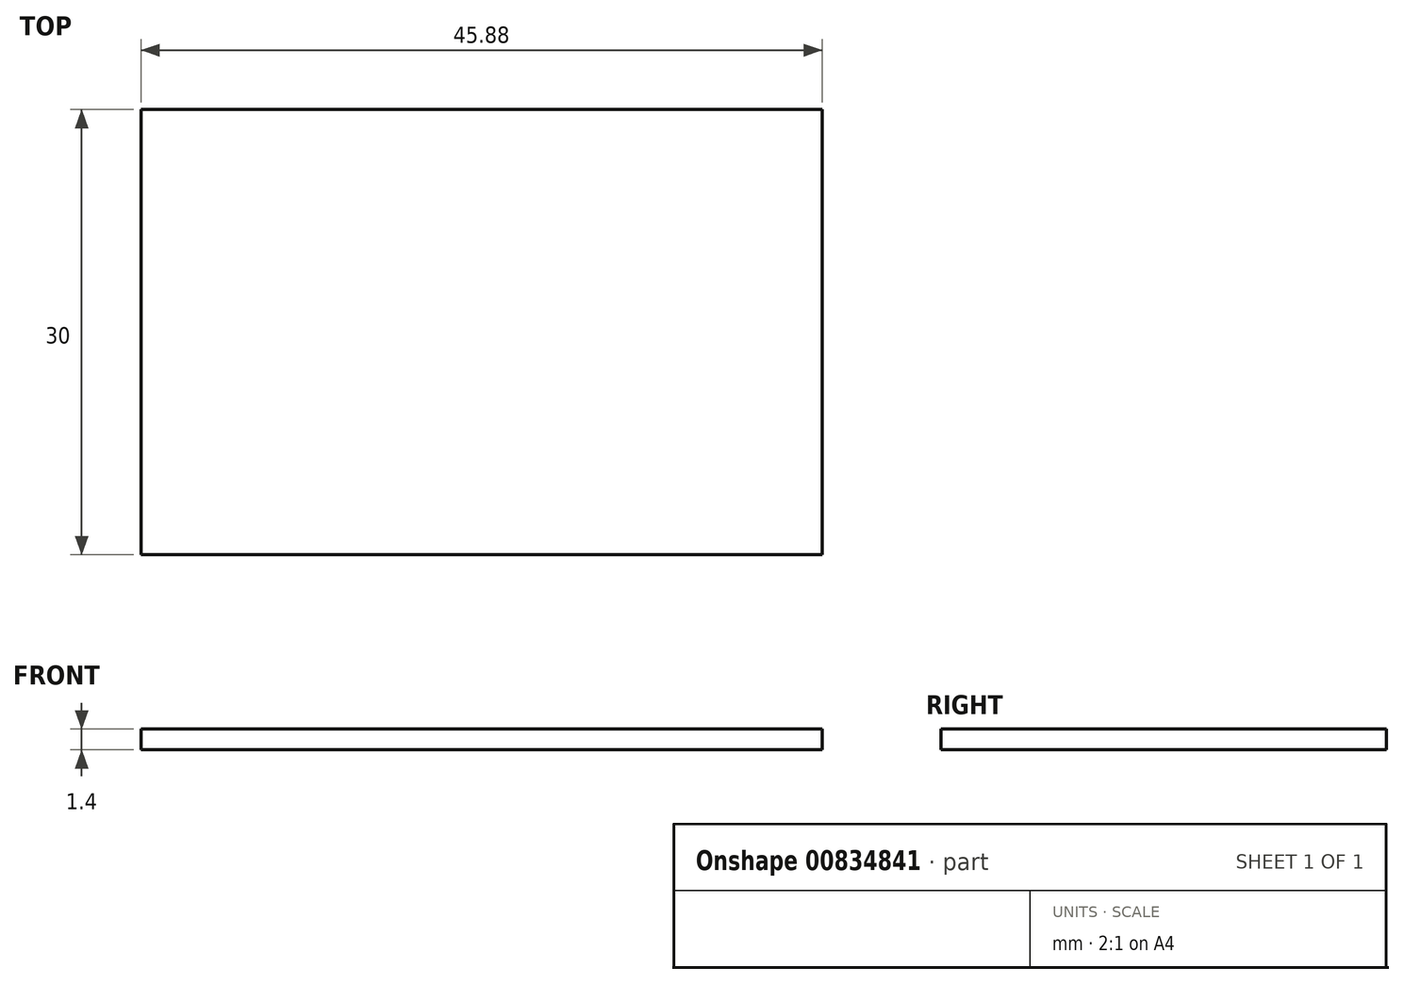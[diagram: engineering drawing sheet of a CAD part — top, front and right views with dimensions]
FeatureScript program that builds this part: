
annotation { "Feature Type Name" : "Feature", "Feature Type Description" : "" }
export const myFeature = defineFeature(function(context is Context, id is Id, definition is map)
    precondition{}
    {
        {
            var Q0;
            Q0=qCreatedBy(makeId("Top.planeOp"),FACE);
            var sketch = newSketch(context, id + "F0", { "sketchPlane" : qUnion([Q0])});
            skLineSegment(sketch, "E0.bottom", {"start": v(0, 0) * mm, "end": v(-45.88, 0) * mm});
            skLineSegment(sketch, "E0.top", {"start": v(0, 30) * mm, "end": v(-45.88, 30) * mm});
            skLineSegment(sketch, "E0.left", {"start": v(0, 0) * mm, "end": v(0, 30) * mm});
            skLineSegment(sketch, "E0.right", {"start": v(-45.88, 0) * mm, "end": v(-45.88, 30) * mm});
            skSolve(sketch);
        }
        {
            var Q0;
            Q0 = qSketchRegion(id + "F0", true);
            extrude(context, id + "F1", {"entities" : qUnion([Q0]), "depth" : 1.4 * mm, "offsetDistance" : 25 * mm});
        }
    });
